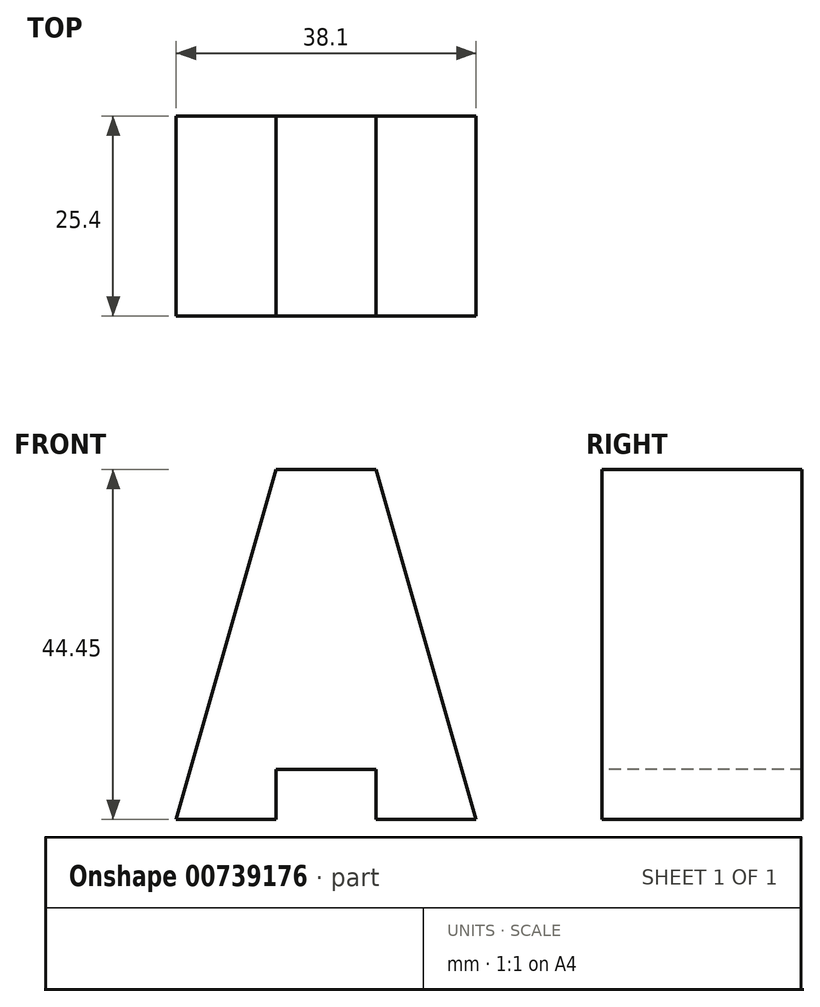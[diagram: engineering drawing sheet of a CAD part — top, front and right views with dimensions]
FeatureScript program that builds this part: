
annotation { "Feature Type Name" : "Feature", "Feature Type Description" : "" }
export const myFeature = defineFeature(function(context is Context, id is Id, definition is map)
    precondition{}
    {
        {
            var Q0;
            Q0=qCreatedBy(makeId("Front.planeOp"),FACE);
            var sketch = newSketch(context, id + "F0", { "sketchPlane" : qUnion([Q0])});
            skLineSegment(sketch, "E0", {"start": v(-20.87, 45.93) * mm, "end": v(17.23, 45.93) * mm});
            skLineSegment(sketch, "E1", {"start": v(17.23, 45.93) * mm, "end": v(17.23, 1.48) * mm});
            skLineSegment(sketch, "E2", {"start": v(17.23, 1.48) * mm, "end": v(-20.87, 1.48) * mm});
            skLineSegment(sketch, "E3", {"start": v(-20.87, 1.48) * mm, "end": v(-20.87, 45.93) * mm});
            skSolve(sketch);
        }
        {
            var Q0;
            Q0=makeQuery(id+"F0.imprint","IMPRINT",FACE,{"disambiguationData":[TD([[makeQuery(id+"F0.imprint","IMPRINT",EDGE,{"derivedFrom":sQuery(id+"F0.wireOp",EDGE,"E0")}),-1.0]])]});
            extrude(context, id + "F1", {"entities" : qUnion([Q0]), "depth" : 25.4 * mm, "offsetDistance" : 25.4 * mm});
        }
        {
            var Q0;
            Q0=makeQuery(id+"F1.opExtrude","CAP_FACE",FACE,{"disambiguationData":[OSD([sQuery(id+"F0.wireOp",EDGE,"E0"),sQuery(id+"F0.wireOp",EDGE,"E1"),sQuery(id+"F0.wireOp",EDGE,"E2"),sQuery(id+"F0.wireOp",EDGE,"E3")])],"isStart":false});
            var sketch = newSketch(context, id + "F2", { "sketchPlane" : qUnion([Q0])});
            skLineSegment(sketch, "E4", {"start": v(4.53, 45.93) * mm, "end": v(17.23, 1.48) * mm});
            skSolve(sketch);
        }
        {
            var Q0;
            Q0 = qSketchRegion(id + "F2", true);
            var Q1;
            {var subQ0=sQuery(id+"F2.wireOp",EDGE,"E4");Q1=makeQuery(id+"F2.imprint","IMPRINT",FACE,{"disambiguationData":[TD([[makeQuery(id+"F2.imprint","IMPRINT",EDGE,{"derivedFrom":subQ0}),1.0]])]});}
            extrude(context, id + "F3", {"entities" : qUnion([Q0, Q1]), "operationType" : NewBodyOperationType.REMOVE, "endBound" : BoundingType.THROUGH_ALL, "oppositeDirection" : true, "depth" : 25.4 * mm, "offsetDistance" : 25.4 * mm});
        }
        {
            var Q0;
            Q0=makeQuery(id+"F1.opExtrude","CAP_FACE",FACE,{"disambiguationData":[OSD([sQuery(id+"F0.wireOp",EDGE,"E0"),sQuery(id+"F0.wireOp",EDGE,"E1"),sQuery(id+"F0.wireOp",EDGE,"E2"),sQuery(id+"F0.wireOp",EDGE,"E3")])],"isStart":false});
            var sketch = newSketch(context, id + "F4", { "sketchPlane" : qUnion([Q0])});
            skLineSegment(sketch, "E5", {"start": v(-8.17, 45.93) * mm, "end": v(-20.87, 1.48) * mm});
            skSolve(sketch);
        }
        {
            var Q0;
            Q0 = qSketchRegion(id + "F4", true);
            var Q1;
            {var subQ0=sQuery(id+"F4.wireOp",EDGE,"E5");Q1=makeQuery(id+"F4.imprint","IMPRINT",FACE,{"disambiguationData":[TD([[makeQuery(id+"F4.imprint","IMPRINT",EDGE,{"derivedFrom":subQ0}),-1.0]])]});}
            extrude(context, id + "F5", {"entities" : qUnion([Q0, Q1]), "operationType" : NewBodyOperationType.REMOVE, "endBound" : BoundingType.THROUGH_ALL, "oppositeDirection" : true, "depth" : 25.4 * mm, "offsetDistance" : 25.4 * mm});
        }
        {
            var Q0;
            Q0=makeQuery(id+"F1.opExtrude","CAP_FACE",FACE,{"disambiguationData":[OSD([sQuery(id+"F0.wireOp",EDGE,"E0"),sQuery(id+"F0.wireOp",EDGE,"E1"),sQuery(id+"F0.wireOp",EDGE,"E2"),sQuery(id+"F0.wireOp",EDGE,"E3")])],"isStart":false});
            var sketch = newSketch(context, id + "F6", { "sketchPlane" : qUnion([Q0])});
            skLineSegment(sketch, "E6", {"start": v(-8.17, 1.48) * mm, "end": v(-8.17, 7.83) * mm});
            skLineSegment(sketch, "E7", {"start": v(-8.17, 7.83) * mm, "end": v(4.53, 7.83) * mm});
            skLineSegment(sketch, "E8", {"start": v(4.53, 7.83) * mm, "end": v(4.53, 1.48) * mm});
            skSolve(sketch);
        }
        {
            var Q0;
            Q0 = qSketchRegion(id + "F6", true);
            var Q1;
            {var subQ0=sQuery(id+"F6.wireOp",EDGE,"E6");Q1=makeQuery(id+"F6.imprint","IMPRINT",FACE,{"disambiguationData":[TD([[makeQuery(id+"F6.imprint","IMPRINT",EDGE,{"derivedFrom":subQ0}),-1.0]])]});}
            extrude(context, id + "F7", {"entities" : qUnion([Q0, Q1]), "operationType" : NewBodyOperationType.REMOVE, "endBound" : BoundingType.THROUGH_ALL, "oppositeDirection" : true, "depth" : 25.4 * mm, "offsetDistance" : 25.4 * mm});
        }
    });
